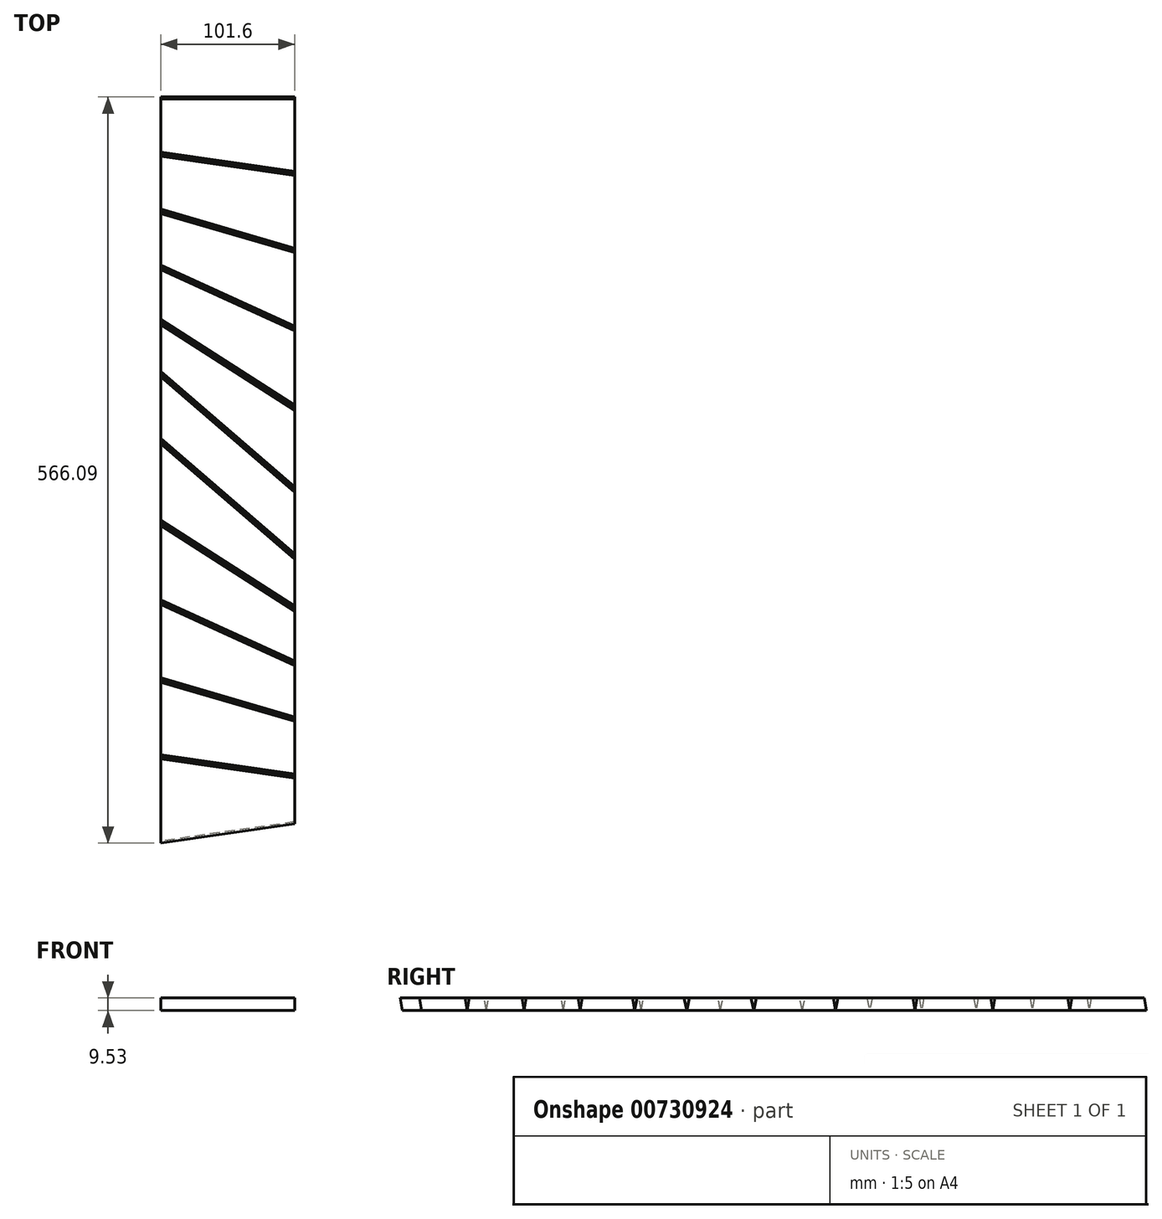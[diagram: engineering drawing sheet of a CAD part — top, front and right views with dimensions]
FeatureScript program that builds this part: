
annotation { "Feature Type Name" : "Feature", "Feature Type Description" : "" }
export const myFeature = defineFeature(function(context is Context, id is Id, definition is map)
    precondition{}
    {
        {
            assignVariable(context, id + "F0", {"name" : "Chamfer", "anyValue" : 9.25});
        }
        {
            var Q0;
            Q0=qCreatedBy(makeId("Top.planeOp"),FACE);
            var sketch = newSketch(context, id + "F1", { "sketchPlane" : qUnion([Q0])});
            skLineSegment(sketch, "E0.bottom", {"start": v(-50.8, 279.4) * mm, "end": v(50.8, 279.4) * mm});
            skLineSegment(sketch, "E0.top", {"start": v(-50.8, -279.4) * mm, "end": v(50.8, -279.4) * mm, "construction": true});
            skLineSegment(sketch, "E0.left", {"start": v(-50.8, 279.4) * mm, "end": v(-50.8, -279.4) * mm});
            skLineSegment(sketch, "E0.right", {"start": v(50.8, 279.4) * mm, "end": v(50.8, -279.4) * mm, "construction": true});
            skPoint(sketch, "E0.middle", {"position": v(0, 0) * mm});
            skLineSegment(sketch, "E1", {"start": v(0, 279.4) * mm, "end": v(0, -279.4) * mm, "construction": true});
            skLineSegment(sketch, "E2", {"start": v(-50.8, 0) * mm, "end": v(50.8, 0) * mm, "construction": true});
            skLineSegment(sketch, "E3", {"start": v(50.8, 221.31) * mm, "end": v(-50.8, 235.89) * mm});
            skLineSegment(sketch, "E4", {"start": v(50.8, 162.92) * mm, "end": v(-50.8, 192.68) * mm});
            skLineSegment(sketch, "E5", {"start": v(50.8, 103.86) * mm, "end": v(-50.8, 150.14) * mm});
            skLineSegment(sketch, "E6", {"start": v(50.8, 43.65) * mm, "end": v(-50.8, 108.75) * mm});
            skPoint(sketch, "E7", {"position": v(0, 177.8) * mm});
            skPoint(sketch, "E8", {"position": v(0, 127) * mm});
            skPoint(sketch, "E9", {"position": v(0, 76.2) * mm});
            skPoint(sketch, "E10", {"position": v(0, 228.6) * mm});
            skLineSegment(sketch, "E11", {"start": v(50.8, -18.47) * mm, "end": v(-50.8, 69.27) * mm});
            skPoint(sketch, "E12", {"position": v(0, 25.4) * mm});
            skLineSegment(sketch, "E13.1.1", {"start": v(-50.8, 18.47) * mm, "end": v(50.8, -69.27) * mm});
            skLineSegment(sketch, "E13.1.2", {"start": v(-50.8, -43.65) * mm, "end": v(50.8, -108.75) * mm});
            skLineSegment(sketch, "E13.1.3", {"start": v(-50.8, -103.86) * mm, "end": v(50.8, -150.14) * mm});
            skLineSegment(sketch, "E13.1.4", {"start": v(-50.8, -162.92) * mm, "end": v(50.8, -192.68) * mm});
            skLineSegment(sketch, "E13.1.5", {"start": v(-50.8, -221.31) * mm, "end": v(50.8, -235.89) * mm});
            skLineSegment(sketch, "E14", {"start": v(50.8, -272.11) * mm, "end": v(-50.8, -286.69) * mm});
            skLineSegment(sketch, "E15", {"start": v(-50.8, -279.4) * mm, "end": v(-50.8, -286.69) * mm});
            skLineSegment(sketch, "E16", {"start": v(50.8, -272.11) * mm, "end": v(50.8, 279.4) * mm});
            skSolve(sketch);
        }
        {
            var Q0;
            {var subQ0=sQuery(id+"F1.wireOp",EDGE,"E0.bottom");Q0=makeQuery(id+"F1.imprint","IMPRINT",FACE,{"disambiguationData":[TD([[makeQuery(id+"F1.imprint","IMPRINT",EDGE,{"derivedFrom":subQ0}),-1.0]])]});}
            extrude(context, id + "F2", {"entities" : qUnion([Q0]), "depth" : 9.52 * mm, "offsetDistance" : 25.4 * mm});
        }
        {
            var Q0;
            {var subQ0=sQuery(id+"F1.wireOp",EDGE,"E3");Q0=makeQuery(id+"F1.imprint","IMPRINT",FACE,{"disambiguationData":[TD([[makeQuery(id+"F1.imprint","IMPRINT",EDGE,{"derivedFrom":subQ0}),1.0]])]});}
            extrude(context, id + "F3", {"entities" : qUnion([Q0]), "depth" : 9.52 * mm, "offsetDistance" : 25.4 * mm});
        }
        {
            var Q0;
            {var subQ0=sQuery(id+"F1.wireOp",EDGE,"E4");Q0=makeQuery(id+"F1.imprint","IMPRINT",FACE,{"disambiguationData":[TD([[makeQuery(id+"F1.imprint","IMPRINT",EDGE,{"derivedFrom":subQ0}),1.0]])]});}
            extrude(context, id + "F4", {"entities" : qUnion([Q0]), "depth" : 9.52 * mm, "offsetDistance" : 25.4 * mm});
        }
        {
            var Q0;
            {var subQ0=sQuery(id+"F1.wireOp",EDGE,"E5");Q0=makeQuery(id+"F1.imprint","IMPRINT",FACE,{"disambiguationData":[TD([[makeQuery(id+"F1.imprint","IMPRINT",EDGE,{"derivedFrom":subQ0}),1.0]])]});}
            extrude(context, id + "F5", {"entities" : qUnion([Q0]), "depth" : 9.52 * mm, "offsetDistance" : 25.4 * mm});
        }
        {
            var Q0;
            {var subQ0=sQuery(id+"F1.wireOp",EDGE,"E6");Q0=makeQuery(id+"F1.imprint","IMPRINT",FACE,{"disambiguationData":[TD([[makeQuery(id+"F1.imprint","IMPRINT",EDGE,{"derivedFrom":subQ0}),1.0]])]});}
            extrude(context, id + "F6", {"entities" : qUnion([Q0]), "depth" : 9.52 * mm, "offsetDistance" : 25.4 * mm});
        }
        {
            var Q0;
            {var subQ0=sQuery(id+"F1.wireOp",EDGE,"E11");Q0=makeQuery(id+"F1.imprint","IMPRINT",FACE,{"disambiguationData":[TD([[makeQuery(id+"F1.imprint","IMPRINT",EDGE,{"derivedFrom":subQ0}),1.0]])]});}
            extrude(context, id + "F7", {"entities" : qUnion([Q0]), "depth" : 9.52 * mm, "offsetDistance" : 25.4 * mm});
        }
        {
            var Q0;
            {var subQ0=sQuery(id+"F1.wireOp",EDGE,"E13.1.1");Q0=makeQuery(id+"F1.imprint","IMPRINT",FACE,{"disambiguationData":[TD([[makeQuery(id+"F1.imprint","IMPRINT",EDGE,{"derivedFrom":subQ0}),-1.0]])]});}
            extrude(context, id + "F8", {"entities" : qUnion([Q0]), "depth" : 9.52 * mm, "offsetDistance" : 25.4 * mm});
        }
        {
            var Q0;
            {var subQ0=sQuery(id+"F1.wireOp",EDGE,"E13.1.2");Q0=makeQuery(id+"F1.imprint","IMPRINT",FACE,{"disambiguationData":[TD([[makeQuery(id+"F1.imprint","IMPRINT",EDGE,{"derivedFrom":subQ0}),-1.0]])]});}
            extrude(context, id + "F9", {"entities" : qUnion([Q0]), "depth" : 9.52 * mm, "offsetDistance" : 25.4 * mm});
        }
        {
            var Q0;
            {var subQ0=sQuery(id+"F1.wireOp",EDGE,"E13.1.3");Q0=makeQuery(id+"F1.imprint","IMPRINT",FACE,{"disambiguationData":[TD([[makeQuery(id+"F1.imprint","IMPRINT",EDGE,{"derivedFrom":subQ0}),-1.0]])]});}
            extrude(context, id + "F10", {"entities" : qUnion([Q0]), "depth" : 9.52 * mm, "offsetDistance" : 25.4 * mm});
        }
        {
            var Q0;
            {var subQ0=sQuery(id+"F1.wireOp",EDGE,"E13.1.4");Q0=makeQuery(id+"F1.imprint","IMPRINT",FACE,{"disambiguationData":[TD([[makeQuery(id+"F1.imprint","IMPRINT",EDGE,{"derivedFrom":subQ0}),-1.0]])]});}
            extrude(context, id + "F11", {"entities" : qUnion([Q0]), "depth" : 9.52 * mm, "offsetDistance" : 25.4 * mm});
        }
        {
            var Q0;
            {var subQ3=sQuery(id+"F1.wireOp",EDGE,"E13.1.5");Q0=makeQuery(id+"F1.imprint","IMPRINT",FACE,{"disambiguationData":[TD([[makeQuery(id+"F1.imprint","IMPRINT",EDGE,{"derivedFrom":subQ3}),-1.0]])]});}
            extrude(context, id + "F12", {"entities" : qUnion([Q0]), "depth" : 9.52 * mm, "offsetDistance" : 25.4 * mm});
        }
        {
            var Q0;
            Q0=makeQuery(id+"F2.opExtrude","CAP_EDGE",EDGE,{"disambiguationData":[OSD([sQuery(id+"F1.wireOp",EDGE,"E3")])],"isStart":false});
            var Q1;
            Q1=makeQuery(id+"F2.opExtrude","CAP_EDGE",EDGE,{"disambiguationData":[OSD([sQuery(id+"F1.wireOp",EDGE,"E0.bottom")])],"isStart":false});
            chamfer(context, id + "F13", {"entities" : qUnion([Q0, Q1]), "chamferType" : ChamferType.OFFSET_ANGLE, "width" : 9.52 * mm, "oppositeDirection" : false, "angle" : (getVariable(context, 'Chamfer')) * degree, "tangentPropagation" : true});
        }
        {
            var Q0;
            Q0=makeQuery(id+"F3.opExtrude","CAP_EDGE",EDGE,{"disambiguationData":[OSD([sQuery(id+"F1.wireOp",EDGE,"E3")])],"isStart":false});
            var Q1;
            Q1=makeQuery(id+"F3.opExtrude","CAP_EDGE",EDGE,{"disambiguationData":[OSD([sQuery(id+"F1.wireOp",EDGE,"E4")])],"isStart":false});
            chamfer(context, id + "F14", {"entities" : qUnion([Q0, Q1]), "chamferType" : ChamferType.OFFSET_ANGLE, "width" : 9.52 * mm, "oppositeDirection" : true, "angle" : (getVariable(context, 'Chamfer')) * degree, "tangentPropagation" : true});
        }
        {
            var Q0;
            Q0=makeQuery(id+"F4.opExtrude","CAP_EDGE",EDGE,{"disambiguationData":[OSD([sQuery(id+"F1.wireOp",EDGE,"E4")])],"isStart":false});
            var Q1;
            Q1=makeQuery(id+"F4.opExtrude","CAP_EDGE",EDGE,{"disambiguationData":[OSD([sQuery(id+"F1.wireOp",EDGE,"E5")])],"isStart":false});
            chamfer(context, id + "F15", {"entities" : qUnion([Q0, Q1]), "chamferType" : ChamferType.OFFSET_ANGLE, "width" : 9.52 * mm, "oppositeDirection" : true, "angle" : (getVariable(context, 'Chamfer')) * degree, "tangentPropagation" : true});
        }
        {
            var Q0;
            Q0=makeQuery(id+"F5.opExtrude","CAP_EDGE",EDGE,{"disambiguationData":[OSD([sQuery(id+"F1.wireOp",EDGE,"E5")])],"isStart":false});
            var Q1;
            Q1=makeQuery(id+"F5.opExtrude","CAP_EDGE",EDGE,{"disambiguationData":[OSD([sQuery(id+"F1.wireOp",EDGE,"E6")])],"isStart":false});
            chamfer(context, id + "F16", {"entities" : qUnion([Q0, Q1]), "chamferType" : ChamferType.OFFSET_ANGLE, "width" : 9.52 * mm, "oppositeDirection" : true, "angle" : (getVariable(context, 'Chamfer')) * degree, "tangentPropagation" : true});
        }
        {
            var Q0;
            Q0=makeQuery(id+"F6.opExtrude","CAP_EDGE",EDGE,{"disambiguationData":[OSD([sQuery(id+"F1.wireOp",EDGE,"E11")])],"isStart":false});
            var Q1;
            Q1=makeQuery(id+"F6.opExtrude","CAP_EDGE",EDGE,{"disambiguationData":[OSD([sQuery(id+"F1.wireOp",EDGE,"E6")])],"isStart":false});
            chamfer(context, id + "F17", {"entities" : qUnion([Q0, Q1]), "chamferType" : ChamferType.OFFSET_ANGLE, "width" : 9.52 * mm, "oppositeDirection" : false, "angle" : (getVariable(context, 'Chamfer')) * degree, "tangentPropagation" : true});
        }
        {
            var Q0;
            Q0=makeQuery(id+"F7.opExtrude","CAP_EDGE",EDGE,{"disambiguationData":[OSD([sQuery(id+"F1.wireOp",EDGE,"E11")])],"isStart":false});
            var Q1;
            Q1=makeQuery(id+"F7.opExtrude","CAP_EDGE",EDGE,{"disambiguationData":[OSD([sQuery(id+"F1.wireOp",EDGE,"E13.1.1")])],"isStart":false});
            chamfer(context, id + "F18", {"entities" : qUnion([Q0, Q1]), "chamferType" : ChamferType.OFFSET_ANGLE, "width" : 9.52 * mm, "oppositeDirection" : true, "angle" : (getVariable(context, 'Chamfer')) * degree, "tangentPropagation" : true});
        }
        {
            var Q0;
            Q0=makeQuery(id+"F8.opExtrude","CAP_EDGE",EDGE,{"disambiguationData":[OSD([sQuery(id+"F1.wireOp",EDGE,"E13.1.1")])],"isStart":false});
            var Q1;
            Q1=makeQuery(id+"F8.opExtrude","CAP_EDGE",EDGE,{"disambiguationData":[OSD([sQuery(id+"F1.wireOp",EDGE,"E13.1.2")])],"isStart":false});
            chamfer(context, id + "F19", {"entities" : qUnion([Q0, Q1]), "chamferType" : ChamferType.OFFSET_ANGLE, "width" : 9.52 * mm, "oppositeDirection" : false, "angle" : (getVariable(context, 'Chamfer')) * degree, "tangentPropagation" : true});
        }
        {
            var Q0;
            Q0=makeQuery(id+"F9.opExtrude","CAP_EDGE",EDGE,{"disambiguationData":[OSD([sQuery(id+"F1.wireOp",EDGE,"E13.1.2")])],"isStart":false});
            var Q1;
            Q1=makeQuery(id+"F9.opExtrude","CAP_EDGE",EDGE,{"disambiguationData":[OSD([sQuery(id+"F1.wireOp",EDGE,"E13.1.3")])],"isStart":false});
            chamfer(context, id + "F20", {"entities" : qUnion([Q0, Q1]), "chamferType" : ChamferType.OFFSET_ANGLE, "width" : 9.52 * mm, "oppositeDirection" : false, "angle" : (getVariable(context, 'Chamfer')) * degree, "tangentPropagation" : true});
        }
        {
            var Q0;
            Q0=makeQuery(id+"F10.opExtrude","CAP_EDGE",EDGE,{"disambiguationData":[OSD([sQuery(id+"F1.wireOp",EDGE,"E13.1.3")])],"isStart":false});
            var Q1;
            Q1=makeQuery(id+"F10.opExtrude","CAP_EDGE",EDGE,{"disambiguationData":[OSD([sQuery(id+"F1.wireOp",EDGE,"E13.1.4")])],"isStart":false});
            chamfer(context, id + "F21", {"entities" : qUnion([Q0, Q1]), "chamferType" : ChamferType.OFFSET_ANGLE, "width" : 9.52 * mm, "oppositeDirection" : false, "angle" : (getVariable(context, 'Chamfer')) * degree, "tangentPropagation" : true});
        }
        {
            var Q0;
            Q0=makeQuery(id+"F11.opExtrude","CAP_EDGE",EDGE,{"disambiguationData":[OSD([sQuery(id+"F1.wireOp",EDGE,"E13.1.4")])],"isStart":false});
            var Q1;
            Q1=makeQuery(id+"F11.opExtrude","CAP_EDGE",EDGE,{"disambiguationData":[OSD([sQuery(id+"F1.wireOp",EDGE,"E13.1.5")])],"isStart":false});
            chamfer(context, id + "F22", {"entities" : qUnion([Q0, Q1]), "chamferType" : ChamferType.OFFSET_ANGLE, "width" : 9.52 * mm, "oppositeDirection" : false, "angle" : (getVariable(context, 'Chamfer')) * degree, "tangentPropagation" : true});
        }
        {
            var Q0;
            Q0=makeQuery(id+"F12.opExtrude","CAP_EDGE",EDGE,{"disambiguationData":[OSD([sQuery(id+"F1.wireOp",EDGE,"E13.1.5")])],"isStart":false});
            chamfer(context, id + "F23", {"entities" : qUnion([Q0]), "chamferType" : ChamferType.OFFSET_ANGLE, "width" : 9.52 * mm, "oppositeDirection" : false, "angle" : (getVariable(context, 'Chamfer')) * degree, "tangentPropagation" : true});
        }
        {
            var Q0;
            Q0=makeQuery(id+"F12.opExtrude","CAP_EDGE",EDGE,{"disambiguationData":[OSD([sQuery(id+"F1.wireOp",EDGE,"E14")])],"isStart":true});
            chamfer(context, id + "F24", {"entities" : qUnion([Q0]), "chamferType" : ChamferType.OFFSET_ANGLE, "width" : 9.52 * mm, "oppositeDirection" : true, "angle" : (getVariable(context, 'Chamfer')) * degree, "tangentPropagation" : true});
        }
    });
